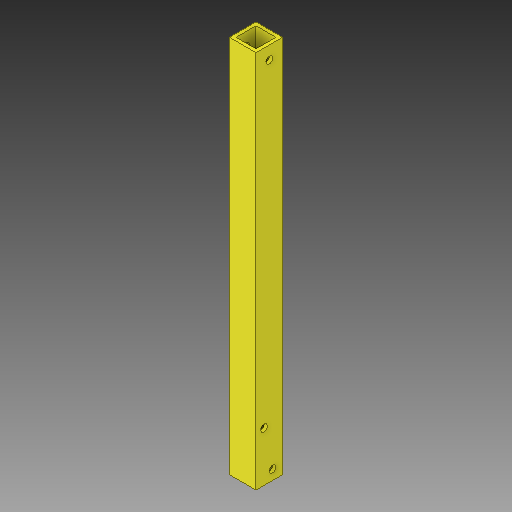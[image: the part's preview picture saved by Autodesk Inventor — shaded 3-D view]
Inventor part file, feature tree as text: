
AUTODESK INVENTOR PART (.ipt)
format: ipt  version: 2017 SP1 (Build 210196100, 196)  size: 114,688 bytes
history: native  units: in
note: dims shown in document units (in); Inventor stores cm internally (conversion verified against a paired STEP export)
features: extrude x2, sketch x2
ambient origin geometry x8: Origin, YZ Plane, XZ Plane, XY Plane, X Axis, Y Axis, Z Axis, Center Point
bodies: Solid1 (feature_tree)
feature tree (4):
  extrude  "Extrusion1"  Depth=0.125in
  extrude  "Extrusion2"  Depth=14.25in
  sketch  "Sketch1"  dims[d0=1.0in d1=0.125in]
  sketch  "Sketch2"  dims[d2=14.25in d3=0.0in d5=0.26in d6=2.375in d9=0.26in d10=11.893in d11=10.0in d12=0.0in d15=0.298in d16=0.5in d17=0.26in d18=0.4375in d19=0.0069in d20=0.375in d22=1.5in d23=0.03in]
